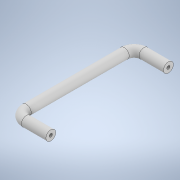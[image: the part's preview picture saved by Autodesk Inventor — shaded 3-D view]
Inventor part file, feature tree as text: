
AUTODESK INVENTOR PART (.ipt)
format: ipt  version: 2021.3 (Build 253353000, 353)  size: 125,440 bytes
history: native  units: mm
features: sketch x3, sweep x1, hole x1
ambient origin geometry x8: Origin, YZ Plane, XZ Plane, XY Plane, X Axis, Y Axis, Z Axis, Center Point
bodies: Volumenkörper1 (feature_tree)
feature tree (5):
  sweep  "Sweeping1"
  hole  "Bohrung1"  [1 undecoded]
  sketch  "Skizze1"  dims[d0=35.0mm d1=120.0mm]
  sketch  "Skizze2"  dims[d2=10.0mm d3=10.0mm]
  sketch  "Skizze3"  dims[d4=0.0mm d5=0.0mm d6=3.242mm d7=8.0mm d8=4.0mm d9=2.0mm d10=90.0deg d11=11.8mm d12=20.594885mm]
note: 1 required parameter value undecoded (feature->parameter linkage not recoverable at this tier; creation-order binding heuristic only, values carry confidence <= 0.55)
